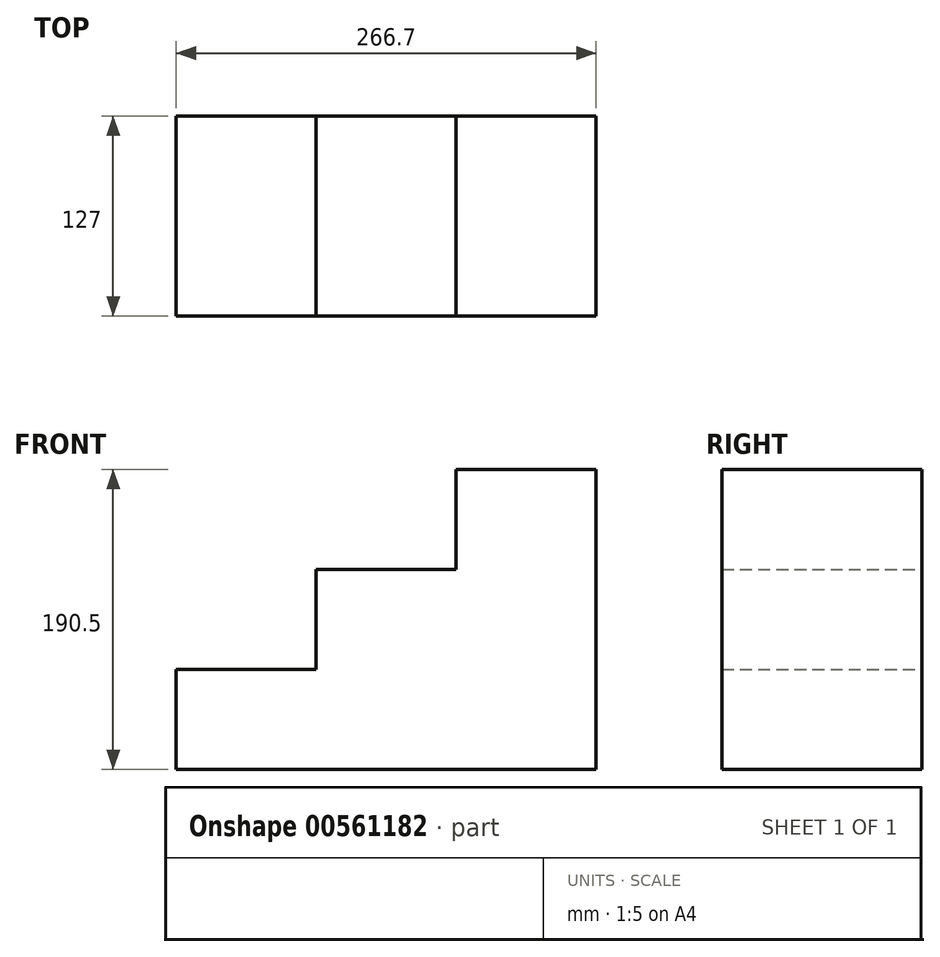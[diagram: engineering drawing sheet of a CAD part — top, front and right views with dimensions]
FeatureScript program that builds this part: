
annotation { "Feature Type Name" : "Feature", "Feature Type Description" : "" }
export const myFeature = defineFeature(function(context is Context, id is Id, definition is map)
    precondition{}
    {
        {
            var Q0;
            Q0=qCreatedBy(makeId("Front.planeOp"),FACE);
            var sketch = newSketch(context, id + "F0", { "sketchPlane" : qUnion([Q0])});
            skLineSegment(sketch, "E0", {"start": v(0, 0) * mm, "end": v(266.7, 0) * mm});
            skLineSegment(sketch, "E1", {"start": v(0, 0) * mm, "end": v(0, 63.5) * mm});
            skLineSegment(sketch, "E2", {"start": v(0, 63.5) * mm, "end": v(88.9, 63.5) * mm});
            skLineSegment(sketch, "E3", {"start": v(88.9, 63.5) * mm, "end": v(88.9, 127) * mm});
            skLineSegment(sketch, "E4", {"start": v(88.9, 127) * mm, "end": v(177.8, 127) * mm});
            skLineSegment(sketch, "E5", {"start": v(177.8, 127) * mm, "end": v(177.8, 190.5) * mm});
            skLineSegment(sketch, "E6", {"start": v(177.8, 190.5) * mm, "end": v(266.7, 190.5) * mm});
            skLineSegment(sketch, "E7", {"start": v(266.7, 190.5) * mm, "end": v(266.7, 0) * mm});
            skSolve(sketch);
        }
        {
            var Q0;
            Q0 = qSketchRegion(id + "F0", true);
            extrude(context, id + "F1", {"entities" : qUnion([Q0]), "depth" : 127 * mm, "offsetDistance" : 25.4 * mm});
        }
    });
